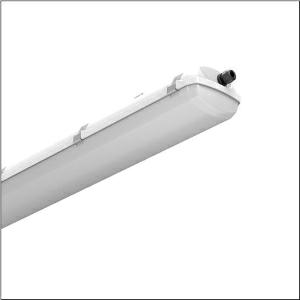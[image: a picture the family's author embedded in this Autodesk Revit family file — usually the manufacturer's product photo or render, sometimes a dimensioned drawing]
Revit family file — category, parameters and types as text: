
# Revit family: monsun_r__ex_51fxa27l840a_cf3b
name_source: partatom
category: Lighting Fixtures
units: mm (PartAtom-declared; Revit-internal decimal feet)

## family parameters
Cut with Voids When Loaded = No
Host = Face
Light Source = No
Part Type = Normal
Room Calculation Point = No
Round Connector Dimension = Use Diameter
Shared = No

## types (1)
- Monsun® Ex (1 x LED, 4650 lm, 30 W, 6500K)
    Apparent Load = 30 VA
    CIE Flux Codes = 46 76 94 98 100
    Color Rendering = 80
    Color Temperature = 6500K
    Default Elevation = 1800 mm
    Description = Monsun® Ex, damp-proof luminaire, primary optical cover: cover, of PC, UV-stabilised, opal, light emission: direct distribution, primary light characteristic: symmetric, installation type: surface-mounted, LED, rated luminous flux: 4.650lm, luminous efficacy: 155lm/W, light colour: 860, colour temperature: 6000K, control gear: ECG, with terminal, 3-pole, max. 2.5mm², through-wiring: 5x 2.5mm², mains connection: 220..250V, AC, 50/60Hz, rated input power: 30W, housing, of PC, light grey (RAL 7035), incl. 1x Ex cable gland M20 for cable diameter 7..12mm with sealing, incl. 1x Ex locking screw M20 with sealing, length: 1.280mm, width: 155mm, height: 105mm, clip for enclosure, of stainless steel, protection rating (complete): IP66, insulation class (complete): insulation class I (protective earthing), certification: CE, explosion class: zone 1,21 II 2G Ex eb mb op is IIC T4 Gb, II 2D Ex tb op is IIIC T67°C Db, impact resistance: IK10, permissible operating ambient temperature: -20..+40°C, contact your sales advisor before using the luminaires in applications with unclear chemical exposure, large temperature fluctuations or condensation-forming humidity, packaging unit: 1 piece
    Height = 105 mm
    Lamp = 1 x LED
    Lamp Light Flux = 4650 lm
    Lamp Power = 30 W
    Lamp count = 1
    Length = 1280 mm
    Luminous efficacy = 155 lm/W
    Manufacturer = Siteco
    ModVariant = No
    Model = 51FXA27L840A
    Mounting Place = Ceiling
    Mounting Type = Surface mounted
    Number of Poles = 1
    OnlyDefault = Yes
    Power Factor = 1
    Product Name = Monsun® Ex
    Product group = damp-proof luminaire
    ProductGroupID = 300
    Protection Class = Protection class I
    Protection Degree = IP 66
    RLX_Detail_Level = 1
    RLX_Emergency_Light_Flux = 0 lm
    RLX_Emergency_Type = 0
    RLX_Emergency_Type_DB = No
    RlxData = <blob elided: 41621 chars, md5=89b6f5ad>
    Socket = socket
    Standby Power = 0 W
    System Light Flux = 4650 lm
    System Power = 30 W
    Type Comments = Product without accessories
    Type Image = l_1258882.jpg
    URL = http://relux.com
    VarID = ---
    Voltage = 0 V
    Weight = 0.00 kg
    Width = 155 mm

## geometry (parser evidence)
native form markers: Blend x4, Sweep x9
no freeform markers — native parametric forms only
